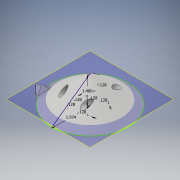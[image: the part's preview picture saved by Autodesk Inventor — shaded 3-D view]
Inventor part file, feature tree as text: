
AUTODESK INVENTOR PART (.ipt)
format: ipt  version: 2018 (Build 220112000, 112)  size: 179,200 bytes
history: native  units: in
note: dims shown in document units (in); Inventor stores cm internally (conversion verified against a paired STEP export)
features: sketch x7, revolve x2, extrude x2, plane x1, loft x1
ambient origin geometry x8: Origin, YZ Plane, XZ Plane, XY Plane, X Axis, Y Axis, Z Axis, Center Point
bodies: Solid1 (feature_tree)
feature tree (13):
  revolve  "Revolution1"  [1 undecoded]
  sketch  "Sketch2"  dims[d0=1.9742in d1=1.4in]
  plane  "Work Plane1"
  loft  "Loft2"
  sketch  "Sketch8"  dims[d6=-0.25in d14=0.0in d15=90.0deg]
  sketch  "Sketch9"  dims[d16=0.0in d17=90.0deg d18=0.128in]
  sketch  "Sketch12"  dims[d19=0.128in d26=0.128in]
  revolve  "Revolution2"  Angle=90.0deg
  extrude  "Extrusion8"  Depth=0.128in
  extrude  "Extrusion9"  Depth=0.128in
  sketch  "Sketch7"  dims[d2=90.0deg d5=0.0817in]
  sketch  "Sketch20"  dims[d27=0.128in]
  sketch  "Sketch21"  dims[d28=0.128in d29=0.128in d30=90.0deg d44=5.0in d45=0.0in d46=0.271in d47=5.0in d48=0.0in]
note: 1 required parameter value undecoded (feature->parameter linkage not recoverable at this tier; creation-order binding heuristic only, values carry confidence <= 0.55)
